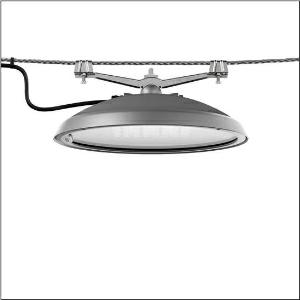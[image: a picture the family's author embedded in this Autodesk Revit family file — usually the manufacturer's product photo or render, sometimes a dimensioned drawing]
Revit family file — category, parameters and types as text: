
# Revit family: dl_r__50_iq_mini___st1_0s_5xa248w41f08ge_d0d2
name_source: partatom
category: Lighting Fixtures
units: mm (PartAtom-declared; Revit-internal decimal feet)

## family parameters
Cut with Voids When Loaded = No
Host = Face
Light Source = No
Part Type = Normal
Room Calculation Point = No
Round Connector Dimension = Use Diameter
Shared = No

## types (1)
- --- (1 x LED, 5190 lm, 31.2 W, 4000K)
    Apparent Load = 31 VA
    CIE Flux Codes = 37 72 97 100 100
    Color Rendering = 70
    Color Temperature = 4000K
    Default Elevation = 1800 mm
    Description = DL® 50 iQ mini, catenary luminaire, primary light control with lens, of PMMA, primary optical cover: cover, of toughened safety glass, transparent, light distribution: ST1.0s, light emission: direct distribution, primary light characteristic: symmetric, installation type: suspended mounting, LED, High Power LED, rated luminous flux: 5.190lm, luminous efficacy: 166lm/W, light colour: 740, colour temperature: 4000K, control: optimised constant luminous flux control (CLO 2.0), Desk-Remote (wireless, voltage-free reading and setting of iQ features in the workshop via application-optimized NFC function/RFID function), Light-Fading, Smart-Wire, Night-Set, Lumen-Switch, Temp-Guard, Auto-Match, Street-Remote, mains connection: 230..240V, AC, 50/60Hz, start of lifetime: 31W, end of service life: 32W, reduction: 15W, luminaire housing, of diecast aluminium, powder-coated, Siteco® metallic grey (DB 702S), diameter: 500mm, height: 115mm, protection rating (complete): IP66, insulation class (complete): insulation class II (safety insulation), certification: CE, ENEC, VDE, impact resistance: IK08, permissible operating ambient temperature for outdoor applications: -25..+40°C, standard-compliant lighting for roads and squares, packaging unit: 1 piece

Light Distribution: ST1.0s
    Height = 124 mm  [stored 0.406824 ft]
    Lamp = 1 x LED
    Lamp Light Flux = 5190 lm
    Lamp Power = 31.2 W
    Lamp count = 1
    Length = 500 mm
    Luminous efficacy = 166 lm/W
    Manufacturer = Siteco
    ModVariant = No
    Model = 5XA248W41F08GE
    Number of Poles = 1
    OnlyDefault = Yes
    Power Factor = 1
    Product Name = DL® 50 iQ mini | ST1.0s
    Product group = catenary luminaire
    ProductGroupID = 6300
    Protection Class = Protection class II
    Protection Degree = IP 66
    RLX_Detail_Level = 1
    RLX_Emergency_Light_Flux = 0 lm
    RLX_Emergency_Type = 0
    RLX_Emergency_Type_DB = No
    RlxData = <blob elided: 123701 chars, md5=003df16a>
    Socket = socket
    Standby Power = 0 W
    System Light Flux = 5190 lm
    System Power = 31 W
    Type Comments = factory setting: luminous flux: 100 % | dim-lin: 254 | 325 mA
    Type Image = l_1242791.jpg
    URL = http://relux.com
    VarID = @adj_072155
    Voltage = 0 V
    Weight = 0.00 kg
    Width = 0 mm  [stored 0 ft]

note: [stored X ft] marks values corroborated as IEEE doubles in the binary element streams (Revit-internal decimal feet)

## geometry (parser evidence)
native form markers: Blend x4, Sweep x14
no freeform markers — native parametric forms only
